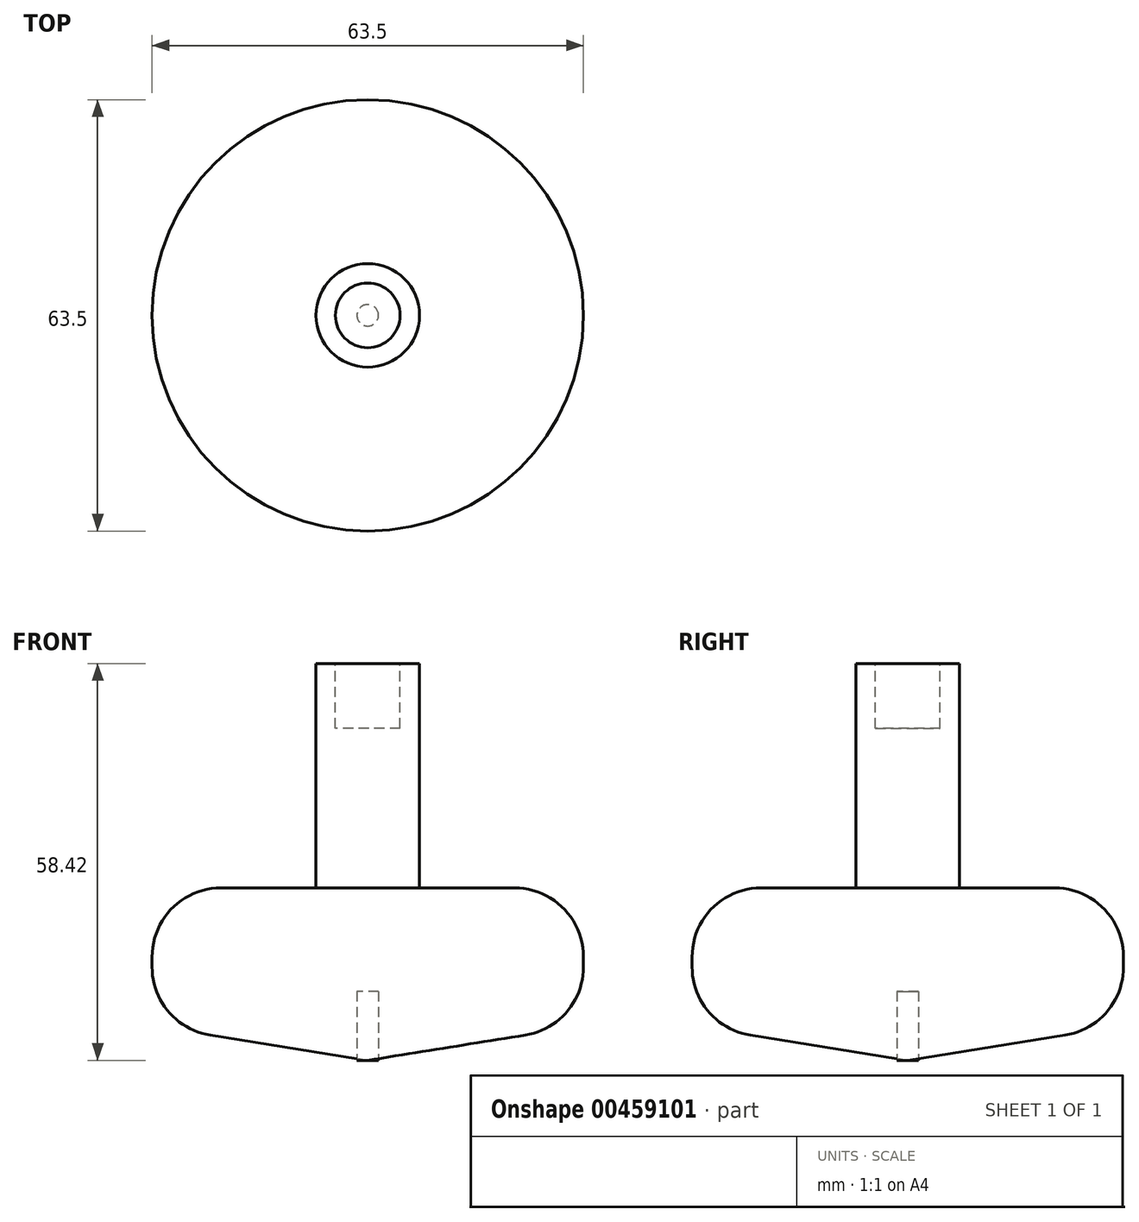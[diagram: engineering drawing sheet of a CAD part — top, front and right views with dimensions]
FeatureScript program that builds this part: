
annotation { "Feature Type Name" : "Feature", "Feature Type Description" : "" }
export const myFeature = defineFeature(function(context is Context, id is Id, definition is map)
    precondition{}
    {
        {
            var Q0;
            Q0=qCreatedBy(makeId("Front.planeOp"),FACE);
            var sketch = newSketch(context, id + "F0", { "sketchPlane" : qUnion([Q0])});
            skLineSegment(sketch, "E0", {"start": v(0, 0) * mm, "end": v(31.75, 5.08) * mm});
            skLineSegment(sketch, "E1", {"start": v(31.75, 5.08) * mm, "end": v(31.75, 25.4) * mm});
            skLineSegment(sketch, "E2", {"start": v(31.75, 25.4) * mm, "end": v(7.62, 25.4) * mm});
            skLineSegment(sketch, "E3", {"start": v(7.62, 25.4) * mm, "end": v(7.62, 58.42) * mm});
            skLineSegment(sketch, "E4", {"start": v(7.62, 58.42) * mm, "end": v(0, 58.42) * mm});
            skLineSegment(sketch, "E5", {"start": v(0, 58.42) * mm, "end": v(0, 0) * mm});
            skSolve(sketch);
        }
        {
            var Q0;
            Q0=makeQuery(id+"F0.imprint","IMPRINT",FACE,{"disambiguationData":[TD([[makeQuery(id+"F0.imprint","IMPRINT",EDGE,{"derivedFrom":sQuery(id+"F0.wireOp",EDGE,"E0")}),1.0]])]});
            var Q1;
            Q1=sQuery(id+"F0.wireOp",EDGE,"E5");
            revolve(context, id + "F1", {"entities" : qUnion([Q0]), "axis" : qUnion([Q1]), "revolveType" : RevolveType.FULL});
        }
        {
            var Q0;
            Q0=makeQuery(id+"F1.opRevolve","SWEPT_FACE",FACE,{"disambiguationData":[OSD([sQuery(id+"F0.wireOp",EDGE,"E1")])]});
            fillet(context, id + "F2", {"entities" : qUnion([Q0]), "radius" : 10.16 * mm, "tangentPropagation" : true, "allowEdgeOverflow" : false});
        }
        {
            var Q0;
            Q0=qCreatedBy(makeId("Top.planeOp"),FACE);
            var sketch = newSketch(context, id + "F3", { "sketchPlane" : qUnion([Q0])});
            skCircle(sketch, "E6", {"center": v(0, 0) * mm, "radius": 1.59 * mm});
            skSolve(sketch);
        }
        {
            var Q0;
            Q0 = qSketchRegion(id + "F3", true);
            extrude(context, id + "F4", {"entities" : qUnion([Q0]), "depth" : 10.16 * mm});
        }
        {
            var Q0;
            Q0=makeQuery(id+"F1.opRevolve","SWEPT_FACE",FACE,{"disambiguationData":[OSD([sQuery(id+"F0.wireOp",EDGE,"E4")])]});
            var sketch = newSketch(context, id + "F5", { "sketchPlane" : qUnion([Q0])});
            skCircle(sketch, "E7", {"center": v(0, 0) * mm, "radius": 4.76 * mm});
            skSolve(sketch);
        }
        {
            var Q0;
            Q0 = qSketchRegion(id + "F5", true);
            extrude(context, id + "F6", {"entities" : qUnion([Q0]), "oppositeDirection" : true, "depth" : 9.52 * mm});
        }
    });
